# Revit family: QF_BOURGEAT_Self_GN4_Meuble_neutre_dessus_decaisse
name_source: partatom
category: Equipement spécialisé
revit_build: Autodesk Revit 2015 (Build: 20140606_1530(x64)
units: mm (PartAtom-declared; Revit-internal decimal feet)

## types (7) — shared parameters
Certification = NF alimentaire
Charge max = 150.00 kg
Fabricant = BOURGEAT
Longueur hors tout = 1710 mm  [stored 5.61024 ft]
Nature isolant = laine de verre
Poids net à vide = 155.00 kg
Profondeur hors tout = 820 mm  [stored 2.69029 ft]
Spécification du Fabricant = Meuble_dessus_decaisse_OASIS
URL catalogue = http://www.bourgeat.fr
lg_etagere = 1238 mm  [stored 4.06168 ft]
lg_pare_haleine = 1260 mm  [stored 4.13386 ft]
lgconsole = 1666 mm  [stored 5.46588 ft]
lgmeuble = 1642 mm

## per-type parameters (varying)
| type | Etageres | Hauteur hors tout | Modèle | Pare_haleine | Pieds | Roues |
| GN4_+_pied | Non | 900 mm | 854124 | Non | Oui | Non |
| GN4_+_etageres | Oui | 1310 mm | 854124+854963 | Non | Oui | Non |
| GN4_+_pare_haleine | Non | 900 mm | 854124+854973 | Oui | Oui | Non |
| GN4_+_roues | Non | 900 mm | 854124+854950 | Non | Non | Oui |
| GN4_+_etageres_+_pare_haleine | Non | 1310 mm | 854124+854950+854974 | Non | Non | Oui |
| GN4_+_roues_+_etageres | Oui | 900 mm | 854124+854950+854964 | Non | Non | Oui |
| GN4_+_roues_+_etageres_+_pare_haleine | Oui | 1310 mm | 854124+854950+854964+854973 | Oui | Non | Oui |

note: [stored X ft] marks values corroborated as IEEE doubles in the binary element streams (Revit-internal decimal feet)

## geometry (parser evidence)
native form markers: Blend x12
no freeform markers — native parametric forms only
